# Revit family: 1030551(n0300)
name_source: partatom
category: Security Devices
units: mm (PartAtom-declared; Revit-internal decimal feet)

## family parameters
Always vertical = No
Cut with Voids When Loaded = No
Host = Ceiling
OmniClass Number = 23.85.30.14
OmniClass Title = Presence Detection/Registration
Room Calculation Point = No
Shared = Yes

## types (2) — shared parameters
zero-valued in all types: A

## per-type parameters (varying)
- Type 1: CTN=0; EF000008=0 mm  [stored 0 ft]; EF000040=0 mm  [stored 0 ft]; EF000049=0 mm  [stored 0 ft]; EF000194=0; EF000218=0 mm  [stored 0 ft]; EF000551=0 mm  [stored 0 ft]; EF000846=0 mm  [stored 0 ft]; EF001322=0 mm  [stored 0 ft]; EF001323=0 mm  [stored 0 ft]; EF003843=0 mm  [stored 0 ft]; EF003882=0; EF004101=0.00°; EF004265=0 mm  [stored 0 ft]; EF006589=0; EF006590=0; EF008011=0 mm  [stored 0 ft]; EF010886=0 mm  [stored 0 ft]; EF010945=0 mm  [stored 0 ft]; EF010946=0 mm  [stored 0 ft]; LOG=0; NOCUPEROU=0; PRICEQUANTITY=0; QUANTITYINT=0; QUANTITYMIN=0
- 1030551: ARTICLENO=NB; BOMINFO=LINA; CATALOG=Theben; COO=HU; CTN=90314990; DEEPLINK_PRODUKTSEITE=http://www.theben.de; DESCLONG=Motion detector for ceiling mounting, detection area round, automatic brightness-dependent control for lighting, mixed light measurement, switch-off delay adjustable, sensitivity adjustable, values preset (can be remotely parameterized); DESCSHORT=Motion detector for ceiling installation, control for lighting; EF000003=EV000384; EF000007=Grey; EF000008=97 mm  [stored 0.318241 ft]; EF000010=Motion detector; EF000025=false; EF000040=71 mm  [stored 0.23294 ft]; EF000049=97 mm  [stored 0.318241 ft]; EF000124=Screw clamp; EF000139=Untreated; EF000147=false; EF000187=AC; EF000194=3600; EF000218=1 mm  [stored 0.00328084 ft]; EF000416=50, 60 Hz; EF000483=false; EF000551=97 mm  [stored 0.318241 ft]; EF000846=1 mm  [stored 0.00328084 ft]; EF001098=true; EF001099=false; EF001198=false; EF001257=Thermoplast; EF001322=4000 mm  [stored 13.1234 ft]; EF001323=4000 mm  [stored 13.1234 ft]; EF001731=-15, 50 °C; EF002169=Plastic; EF003429=true; EF003808=false; EF003814=5, 3000 lx; EF003832=false; EF003843=8000 mm; EF003848=true; EF003858=false; EF003863=false; EF003876=false; EF003882=7005; EF003890=false; EF003898=true; EF003904=true; EF003920=false; EF004101=360.00°; EF004265=15 mm  [stored 0.0492126 ft]; EF004293=IK04; EF005474=IP54; EF005624=false; EF006243=false; EF006311=false; EF006569=matt; EF006582=0, 360 °; EF006589=10; EF006590=60; EF006644=false; EF007575=true; EF008011=2500 mm  [stored 8.2021 ft]; EF009569=false; EF010886=58 mm  [stored 0.190289 ft]; EF010945=96 mm  [stored 0.314961 ft]; EF010946=55 mm  [stored 0.180446 ft]; EF011072=false; EF011991=false; EF014925=false; EF014926=false; EF014927=false; EF020270=Passive infrared; EF021180=true; EF023790=false; GEBRAUCHSANLEITUNG=http://www.theben.de; INTNO=7612748005020; LINA=1030551; LOG=300; MANUID=1030551; MANUNAME=Theben AG; MANUTYPEDESC=theMova S360-100 AP GR; Manufacturer=Theben; Model=1030551; NB=1030551(N0300); NBSYN=$MANUID.($SA.$A.$LOG.); NN=theMova S; NOCUPEROU=1; PRICEQUANTITY=1; PRODUKTDATENBLATT=http://www.theben.de; QUANTITYINT=1; QUANTITYMIN=1; REACH_ERKLAERUNG=http://www.theben.de; REMARKS=ERP-GROUP 345; SA=None; SUPPLIER=THEBEN; SUPPLIERALTNO=1030551

note: [stored X ft] marks values corroborated as IEEE doubles in the binary element streams (Revit-internal decimal feet)

## geometry (parser evidence)
native form markers: Sweep x7
no freeform markers — native parametric forms only
